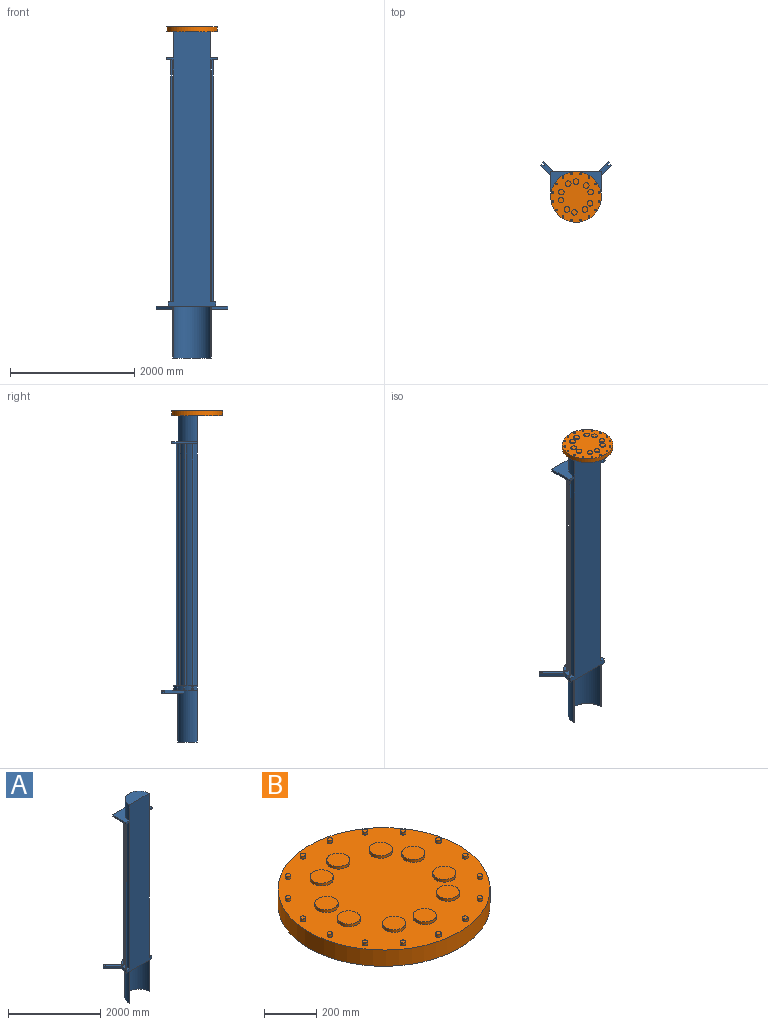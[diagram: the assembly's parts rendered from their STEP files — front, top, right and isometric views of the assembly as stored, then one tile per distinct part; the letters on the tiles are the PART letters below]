
ASSEMBLY  parts=2 mates=1
PART A: 78 faces, bbox 1149.5x574.7x5248.3 mm
  f0: cylinder r=304.8mm len=3886.2mm, axis (0,0,-1), area 3721259.7mm2, adj f7,f12,f77
  f1: cylinder r=304.8mm len=828.68mm, axis (0,0,-1), area 793503.9mm2, adj f6,f8,f77
  f2: plane 762x381mm, normal (0,0,-1), area 65639.9mm2, adj f3,f4,f5,f15,f16,f17,f18,f19
  f3: cylinder r=381mm len=76.2mm, axis (0,0,-1), area 4862.2mm2, adj f2,f7,f22,f77
  f4: cylinder r=381mm len=76.2mm, axis (0,0,-1), area 4862.2mm2, adj f2,f7,f41,f77
  f5: cylinder r=309.56mm len=828.68mm, axis (0,0,1), area 805902.4mm2, adj f2,f6,f77
  f6: plane 619.13x309.56mm, normal (0,0,-1), area 4596mm2, adj f1,f5,f77
  f7: plane 762x381mm, normal (0,0,1), area 73269.3mm2, adj f0,f3,f4,f15,f16,f17,f18,f19
  f8: plane 609.6x304.8mm, normal (0,0,-1), area 145931.8mm2, adj f1,f77
  f9: plane 406.4x38.1mm, normal (1,0,0), area 15483.8mm2, adj f11,f12,f76,f77
  f10: plane 406.4x38.1mm, normal (-1,0,0), area 15483.8mm2, adj f11,f12,f76,f77
  f11: plane 812.8x406.4mm, normal (0,0,1), area 184390.2mm2, adj f9,f10,f14,f76,f77
  f12: plane 812.8x406.4mm, normal (0,0,-1), area 181714.1mm2, adj f0,f9,f10,f68,f69,f70,f71,f72
  f13: plane 609.6x304.8mm, normal (0,0,1), area 145931.8mm2, adj f14,f77
  f14: cylinder r=304.8mm len=609.6mm, axis (0,0,-1), area 401312.3mm2, adj f11,f13,f77
  f15: cylinder r=10.32mm len=76.2mm, axis (0,0,-1), area 1233.9mm2, adj f2,f7,f41,f75
  f16: plane 76.2x41.07mm, normal (0.21,-0.98,0), area 3200.9mm2, adj f2,f7,f42,f75
  f17: cylinder r=10.32mm len=76.2mm, axis (0,0,-1), area 1233.9mm2, adj f2,f7,f43,f74
  f18: plane 76.2x34.57mm, normal (0.57,-0.82,0), area 3200.9mm2, adj f2,f7,f44,f74
  f19: plane 76.2x35.28mm, normal (0.84,-0.54,0), area 3200.9mm2, adj f2,f7,f31,f73
  f20: cylinder r=10.32mm len=76.2mm, axis (0,0,-1), area 1233.9mm2, adj f2,f7,f45,f73
  f21: cylinder r=10.32mm len=76.2mm, axis (0,0,-1), area 1233.9mm2, adj f2,f7,f40,f72
  f22: plane 76.2x41.32mm, normal (0.18,0.98,0), area 3200.9mm2, adj f2,f3,f7,f72
  f23: cylinder r=10.32mm len=76.2mm, axis (0,0,-1), area 1233.9mm2, adj f2,f7,f38,f71
  f24: plane 76.2x34.33mm, normal (0.57,0.82,0), area 3178.7mm2, adj f2,f7,f39,f71
  f25: cylinder r=10.32mm len=76.2mm, axis (0,0,-1), area 1233.9mm2, adj f2,f7,f36,f70
  f26: plane 76.2x34.57mm, normal (0.82,0.57,0), area 3200.9mm2, adj f2,f7,f37,f70
  f27: cylinder r=10.32mm len=76.2mm, axis (0,0,-1), area 1233.9mm2, adj f2,f7,f32,f69
  f28: plane 76.2x40.78mm, normal (0.98,-0.21,0), area 3178.7mm2, adj f2,f7,f33,f69
  f29: cylinder r=10.32mm len=76.2mm, axis (0,0,-1), area 1233.9mm2, adj f2,f7,f34,f68
  f30: plane 76.2x41.07mm, normal (0.98,0.21,0), area 3200.9mm2, adj f2,f7,f35,f68
  f31: cylinder r=381mm len=117.35mm, axis (0,0,-1), area 9724.4mm2, adj f2,f7,f19,f32
  f32: plane 76.2x43.46mm, normal (-0.98,0.21,0), area 3387.4mm2, adj f2,f7,f27,f31
  f33: cylinder r=381mm len=129.71mm, axis (0,0,-1), area 9932.3mm2, adj f2,f7,f28,f34
  f34: plane 76.2x43.5mm, normal (-0.98,-0.21,0), area 3390.3mm2, adj f2,f7,f29,f33
  f35: cylinder r=381mm len=117.35mm, axis (0,0,-1), area 9724.4mm2, adj f2,f7,f30,f36
  f36: plane 76.2x37.34mm, normal (-0.84,-0.54,0), area 3387.4mm2, adj f2,f7,f25,f35
  f37: cylinder r=381mm len=89.82mm, axis (0,0,-1), area 9724.4mm2, adj f2,f7,f26,f38,f65
  f38: plane 76.2x36.58mm, normal (-0.57,-0.82,0), area 3387.4mm2, adj f2,f7,f23,f37
  f39: cylinder r=381mm len=118.51mm, axis (0,0,-1), area 9828.4mm2, adj f2,f7,f24,f40
  f40: plane 76.2x43.46mm, normal (-0.21,-0.98,0), area 3387.4mm2, adj f2,f7,f21,f39
  f41: plane 76.2x43.73mm, normal (-0.18,0.98,0), area 3387.4mm2, adj f2,f4,f7,f15
  f42: cylinder r=381mm len=118.51mm, axis (0,0,-1), area 9828.4mm2, adj f2,f7,f16,f43
  f43: plane 76.2x36.61mm, normal (-0.57,0.82,0), area 3390.3mm2, adj f2,f7,f17,f42
  f44: cylinder r=381mm len=89.82mm, axis (0,0,-1), area 9724.4mm2, adj f2,f7,f18,f45,f55
  f45: plane 76.2x36.58mm, normal (-0.82,0.57,0), area 3387.4mm2, adj f2,f7,f20,f44
  f46: cylinder r=13.49mm len=44.45mm, axis (0,0,1), area 1873.3mm2, adj f47,f53,f54,f55
  f47: plane 44.45x27.03mm, normal (0.71,-0.71,0), area 1699mm2, adj f46,f48,f54,f55
  f48: plane 44.45x17.4mm, normal (0.71,0.71,0), area 1093.8mm2, adj f47,f49,f54,f55
  f49: plane 305.33x305.33mm, normal (-0.71,0.71,0), area 19012.1mm2, adj f2,f48,f50,f54,f55,f67
  f50: plane 53.88x53.88mm, normal (-0.71,-0.71,0), area 1935.5mm2, adj f2,f49,f51,f67
  f51: plane 305.33x305.33mm, normal (0.71,-0.71,0), area 19012.1mm2, adj f2,f50,f52,f54,f55,f67
  f52: plane 44.45x17.15mm, normal (0.71,0.71,0), area 1078.2mm2, adj f51,f53,f54,f55
  f53: plane 44.45x27.28mm, normal (-0.7,0.71,0), area 1699.1mm2, adj f46,f52,f54,f55
  f54: plane 345.74x345.74mm, normal (0,0,-1), area 30130.7mm2, adj f46,f47,f48,f49,f51,f52,f53,f67
  f55: plane 333.62x333.62mm, normal (0,0,1), area 28727.5mm2, adj f44,f46,f47,f48,f49,f51,f52,f53
  f56: cylinder r=13.49mm len=44.45mm, axis (0,0,1), area 1873.3mm2, adj f57,f63,f64,f65
  f57: plane 44.45x27.28mm, normal (0.7,0.71,0), area 1699.1mm2, adj f56,f58,f64,f65
  f58: plane 44.45x17.15mm, normal (-0.71,0.71,0), area 1078.2mm2, adj f57,f59,f64,f65
  f59: plane 305.33x305.33mm, normal (-0.71,-0.71,0), area 19012.1mm2, adj f2,f58,f60,f64,f65,f66
  f60: plane 53.88x53.88mm, normal (0.71,-0.71,0), area 1935.5mm2, adj f2,f59,f61,f66
  f61: plane 305.33x305.33mm, normal (0.71,0.71,0), area 19012.1mm2, adj f2,f60,f62,f64,f65,f66
  f62: plane 44.45x17.4mm, normal (-0.71,0.71,0), area 1093.8mm2, adj f61,f63,f64,f65
  f63: plane 44.45x27.03mm, normal (-0.71,-0.71,0), area 1699mm2, adj f56,f62,f64,f65
  f64: plane 345.74x345.74mm, normal (0,0,-1), area 30130.7mm2, adj f56,f57,f58,f59,f61,f62,f63,f66
  f65: plane 333.62x333.62mm, normal (0,0,1), area 28727.5mm2, adj f37,f56,f57,f58,f59,f61,f62,f63
  f66: plane 67.35x67.35mm, normal (0.5,-0.5,-0.71), area 2052.9mm2, adj f59,f60,f61,f64
  f67: plane 67.35x67.35mm, normal (-0.5,-0.5,-0.71), area 2052.9mm2, adj f49,f50,f51,f54
  f68: cylinder r=10.32mm len=3962.4mm, axis (0,0,-1), area 255478.1mm2, adj f2,f7,f12,f29,f30
  f69: cylinder r=10.32mm len=3962.4mm, axis (0,0,-1), area 255452.4mm2, adj f2,f7,f12,f27,f28
  f70: cylinder r=10.32mm len=3962.4mm, axis (0,0,-1), area 255478.1mm2, adj f2,f7,f12,f25,f26
  f71: cylinder r=10.32mm len=3962.4mm, axis (0,0,-1), area 255452.4mm2, adj f2,f7,f12,f23,f24
  f72: cylinder r=10.32mm len=3962.4mm, axis (0,0,-1), area 255478.1mm2, adj f2,f7,f12,f21,f22
  f73: cylinder r=10.32mm len=3962.4mm, axis (0,0,-1), area 255478.1mm2, adj f2,f7,f12,f19,f20
  f74: cylinder r=10.32mm len=3962.4mm, axis (0,0,-1), area 255478.1mm2, adj f2,f7,f12,f17,f18
  f75: cylinder r=10.32mm len=3962.4mm, axis (0,0,-1), area 255478.1mm2, adj f2,f7,f12,f15,f16
  f76: plane 812.8x38.1mm, normal (0,1,0), area 30967.7mm2, adj f9,f10,f11,f12
  f77: plane 5248.28x812.8mm, normal (0,-1,0), area 2721436.1mm2, adj f0,f1,f2,f3,f4,f5,f6,f7
PART B: 55 faces, bbox 812.8x812.8x88.9 mm
  f0: cylinder r=10.32mm len=20.64mm, axis (0,0,-1), area 823.4mm2, adj f1,f29
  f1: plane 20.64x20.64mm, normal (0,0,1), area 334.5mm2, adj f0
  f2: cylinder r=10.32mm len=20.64mm, axis (0,0,-1), area 823.4mm2, adj f3,f29
  f3: plane 20.64x20.64mm, normal (0,0,1), area 334.5mm2, adj f2
  f4: cylinder r=10.32mm len=20.64mm, axis (0,0,-1), area 823.4mm2, adj f5,f29
  f5: plane 20.64x20.64mm, normal (0,0,1), area 334.5mm2, adj f4
  f6: cylinder r=10.32mm len=20.64mm, axis (0,0,-1), area 823.4mm2, adj f7,f29
  f7: plane 20.64x20.64mm, normal (0,0,1), area 334.5mm2, adj f6
  f8: cylinder r=10.32mm len=20.64mm, axis (0,0,-1), area 823.4mm2, adj f9,f29
  f9: plane 20.64x20.64mm, normal (0,0,1), area 334.5mm2, adj f8
  f10: cylinder r=10.32mm len=20.64mm, axis (0,0,-1), area 823.4mm2, adj f11,f29
  f11: plane 20.64x20.64mm, normal (0,0,1), area 334.5mm2, adj f10
  f12: cylinder r=10.32mm len=20.64mm, axis (0,0,-1), area 823.4mm2, adj f13,f29
  f13: plane 20.64x20.64mm, normal (0,0,1), area 334.5mm2, adj f12
  f14: cylinder r=10.32mm len=20.64mm, axis (0,0,-1), area 823.4mm2, adj f15,f29
  f15: plane 20.64x20.64mm, normal (0,0,1), area 334.5mm2, adj f14
  f16: cylinder r=10.32mm len=20.64mm, axis (0,0,-1), area 823.4mm2, adj f17,f29
  f17: plane 20.64x20.64mm, normal (0,0,1), area 334.5mm2, adj f16
  f18: cylinder r=10.32mm len=20.64mm, axis (0,0,-1), area 823.4mm2, adj f19,f29
  f19: plane 20.64x20.64mm, normal (0,0,1), area 334.5mm2, adj f18
  f20: cylinder r=10.32mm len=20.64mm, axis (0,0,-1), area 823.4mm2, adj f21,f29
  f21: plane 20.64x20.64mm, normal (0,0,1), area 334.5mm2, adj f20
  f22: cylinder r=10.32mm len=20.64mm, axis (0,0,-1), area 823.4mm2, adj f23,f29
  f23: plane 20.64x20.64mm, normal (0,0,1), area 334.5mm2, adj f22
  f24: cylinder r=10.32mm len=20.64mm, axis (0,0,-1), area 823.4mm2, adj f25,f29
  f25: plane 20.64x20.64mm, normal (0,0,1), area 334.5mm2, adj f24
  f26: cylinder r=10.32mm len=20.64mm, axis (0,0,-1), area 823.4mm2, adj f27,f29
  f27: plane 20.64x20.64mm, normal (0,0,1), area 334.5mm2, adj f26
  f28: cylinder r=406.4mm len=812.8mm, axis (0,0,-1), area 194575.7mm2, adj f29,f54
  f29: plane 812.8x812.8mm, normal (0,0,1), area 451444.7mm2, adj f0,f2,f4,f6,f8,f10,f12,f14
  f30: cylinder r=10.32mm len=20.64mm, axis (0,0,-1), area 823.4mm2, adj f29,f31
  f31: plane 20.64x20.64mm, normal (0,0,1), area 334.5mm2, adj f30
  f32: cylinder r=44.45mm len=88.9mm, axis (0,0,-1), area 3547mm2, adj f29,f33
  f33: plane 88.9x88.9mm, normal (0,0,1), area 6207.2mm2, adj f32
  f34: cylinder r=10.32mm len=20.64mm, axis (0,0,-1), area 823.4mm2, adj f29,f35
  f35: plane 20.64x20.64mm, normal (0,0,1), area 334.5mm2, adj f34
  f36: cylinder r=44.45mm len=88.9mm, axis (0,0,-1), area 3547mm2, adj f29,f37
  f37: plane 88.9x88.9mm, normal (0,0,1), area 6207.2mm2, adj f36
  f38: cylinder r=44.45mm len=88.9mm, axis (0,0,-1), area 3547mm2, adj f29,f39
  f39: plane 88.9x88.9mm, normal (0,0,1), area 6207.2mm2, adj f38
  f40: cylinder r=44.45mm len=88.9mm, axis (0,0,-1), area 3547mm2, adj f29,f41
  f41: plane 88.9x88.9mm, normal (0,0,1), area 6207.2mm2, adj f40
  f42: cylinder r=44.45mm len=88.9mm, axis (0,0,-1), area 3547mm2, adj f29,f43
  f43: plane 88.9x88.9mm, normal (0,0,1), area 6207.2mm2, adj f42
  f44: cylinder r=44.45mm len=88.9mm, axis (0,0,-1), area 3547mm2, adj f29,f45
  f45: plane 88.9x88.9mm, normal (0,0,1), area 6207.2mm2, adj f44
  f46: cylinder r=44.45mm len=88.9mm, axis (0,0,-1), area 3547mm2, adj f29,f47
  f47: plane 88.9x88.9mm, normal (0,0,1), area 6207.2mm2, adj f46
  f48: cylinder r=44.45mm len=88.9mm, axis (0,0,-1), area 3547mm2, adj f29,f49
  f49: plane 88.9x88.9mm, normal (0,0,1), area 6207.2mm2, adj f48
  f50: cylinder r=44.45mm len=88.9mm, axis (0,0,-1), area 3547mm2, adj f29,f51
  f51: plane 88.9x88.9mm, normal (0,0,1), area 6207.2mm2, adj f50
  f52: cylinder r=44.45mm len=88.9mm, axis (0,0,-1), area 3547mm2, adj f29,f53
  f53: plane 88.9x88.9mm, normal (0,0,1), area 6207.2mm2, adj f52
  f54: plane 812.8x812.8mm, normal (0,0,-1), area 518868.5mm2, adj f28
PLACE A t=(-490.17,-90.23,-3714.48)mm
PLACE B t=(-490.17,-90.23,959.12)mm
MATE fastened A.f0 <-> B.f28  axis (0,0,1) through (-490.17,-90.23,959.12)mm
